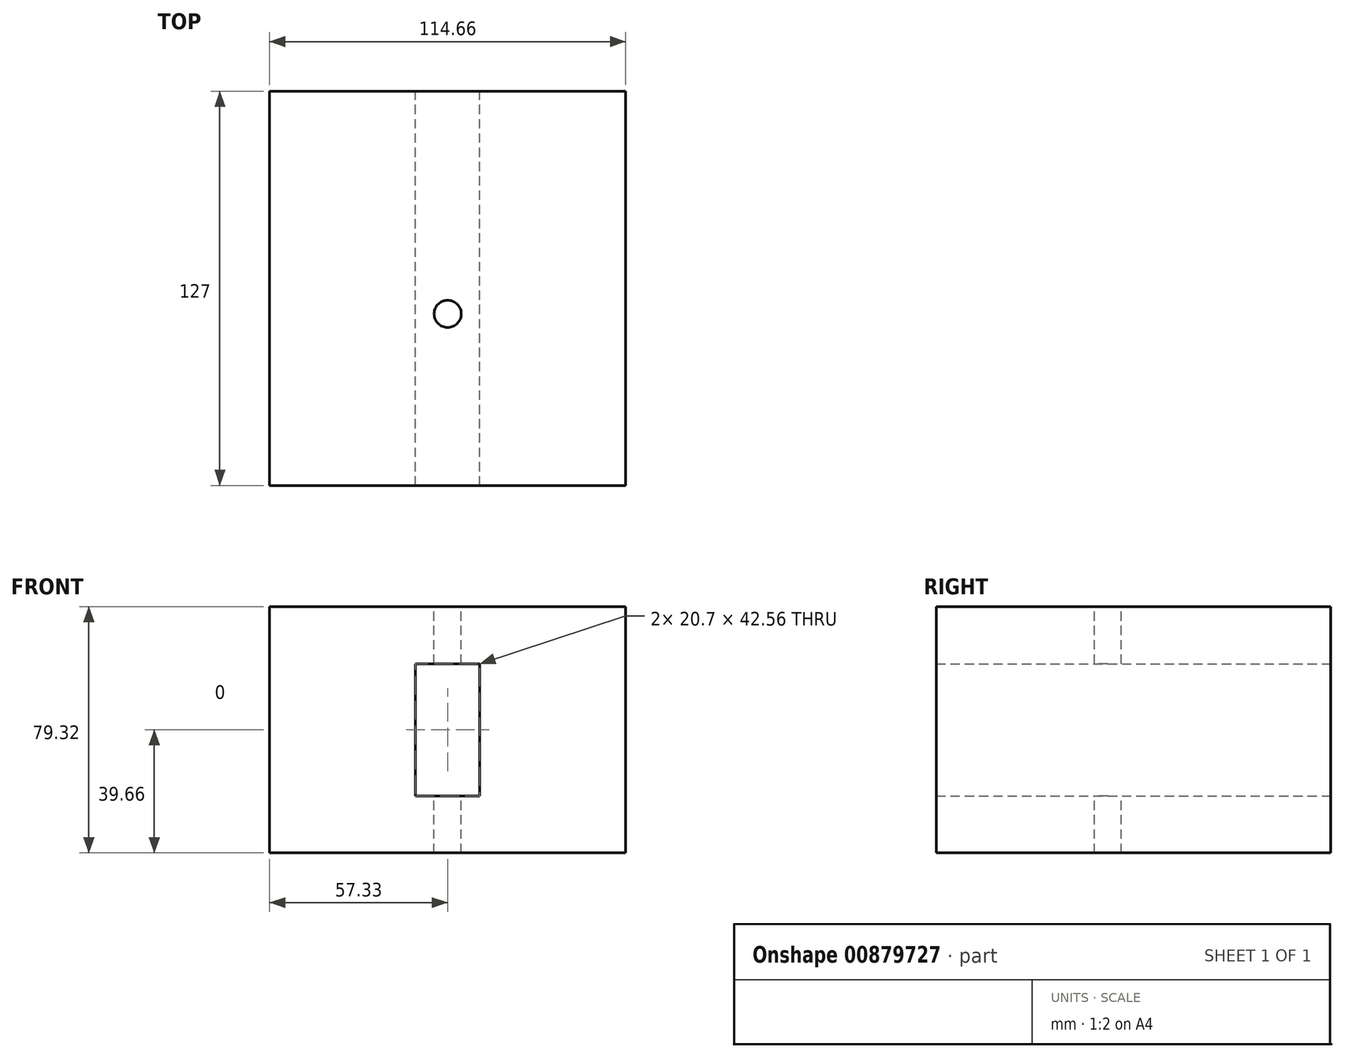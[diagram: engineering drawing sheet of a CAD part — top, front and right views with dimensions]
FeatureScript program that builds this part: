
annotation { "Feature Type Name" : "Feature", "Feature Type Description" : "" }
export const myFeature = defineFeature(function(context is Context, id is Id, definition is map)
    precondition{}
    {
        {
            var Q0;
            Q0=qCreatedBy(makeId("Front.planeOp"),FACE);
            var sketch = newSketch(context, id + "F0", { "sketchPlane" : qUnion([Q0])});
            skLineSegment(sketch, "E0.bottom", {"start": v(-57.33, 39.66) * mm, "end": v(57.33, 39.66) * mm});
            skLineSegment(sketch, "E0.top", {"start": v(-57.33, -39.66) * mm, "end": v(57.33, -39.66) * mm});
            skLineSegment(sketch, "E0.left", {"start": v(-57.33, 39.66) * mm, "end": v(-57.33, -39.66) * mm});
            skLineSegment(sketch, "E0.right", {"start": v(57.33, 39.66) * mm, "end": v(57.33, -39.66) * mm});
            skPoint(sketch, "E0.middle", {"position": v(0, 0) * mm});
            skLineSegment(sketch, "E1.bottom", {"start": v(10.35, 21.28) * mm, "end": v(-10.35, 21.28) * mm});
            skLineSegment(sketch, "E1.top", {"start": v(10.35, -21.28) * mm, "end": v(-10.35, -21.28) * mm});
            skLineSegment(sketch, "E1.left", {"start": v(10.35, 21.28) * mm, "end": v(10.35, -21.28) * mm});
            skLineSegment(sketch, "E1.right", {"start": v(-10.35, 21.28) * mm, "end": v(-10.35, -21.28) * mm});
            skSolve(sketch);
        }
        {
            var Q0;
            Q0=makeQuery(id+"F0.imprint","IMPRINT",FACE,{"disambiguationData":[TD([[makeQuery(id+"F0.imprint","IMPRINT",EDGE,{"derivedFrom":sQuery(id+"F0.wireOp",EDGE,"E0.bottom")}),-1.0]])]});
            extrude(context, id + "F1", {"entities" : qUnion([Q0]), "depth" : 127 * mm, "offsetDistance" : 25.4 * mm});
        }
        {
            var Q0;
            Q0=makeQuery(id+"F1.opExtrude","SWEPT_FACE",FACE,{"disambiguationData":[OSD([sQuery(id+"F0.wireOp",EDGE,"E0.bottom")])]});
            var sketch = newSketch(context, id + "F2", { "sketchPlane" : qUnion([Q0])});
            skPoint(sketch, "E2", {"position": v(0, -71.71) * mm});
            skSolve(sketch);
        }
        {
            var Q0;
            Q0=sQuery(id+"F2.wireOp",VERTEX,"E2");
            var Q1;
            Q1=makeQuery(id+"F1.opExtrude","SWEPT_BODY",BODY,{"disambiguationData":[OSD([sQuery(id+"F0.wireOp",EDGE,"E0.bottom"),sQuery(id+"F0.wireOp",EDGE,"E0.top"),sQuery(id+"F0.wireOp",EDGE,"E0.left"),sQuery(id+"F0.wireOp",EDGE,"E0.right"),sQuery(id+"F0.wireOp",EDGE,"E1.bottom"),sQuery(id+"F0.wireOp",EDGE,"E1.top"),sQuery(id+"F0.wireOp",EDGE,"E1.left"),sQuery(id+"F0.wireOp",EDGE,"E1.right")])]});
            hole(context, id + "F3", {"style" : HoleStyle.SIMPLE, "endStyle" : HoleEndStyle.THROUGH, "standardTappedOrClearance" : lookupTablePath({ "fit" : "Normal (ASME)", "standard" : "ANSI", "size" : "5/16", "type" : "Clearance" }), "standardBlindInLast" : lookupTablePath({ "fit" : "Normal", "standard" : "ANSI", "size" : "5/16", "type" : "Clearance" }), "holeDiameter" : 8.74 * mm, "majorDiameter" : 6.35 * mm, "isTappedThrough" : true, "tappedDepth" : 12.7 * mm, "tapClearance" : 3, "locations" : qUnion([Q0]), "scope" : qUnion([Q1])});
        }
    });
